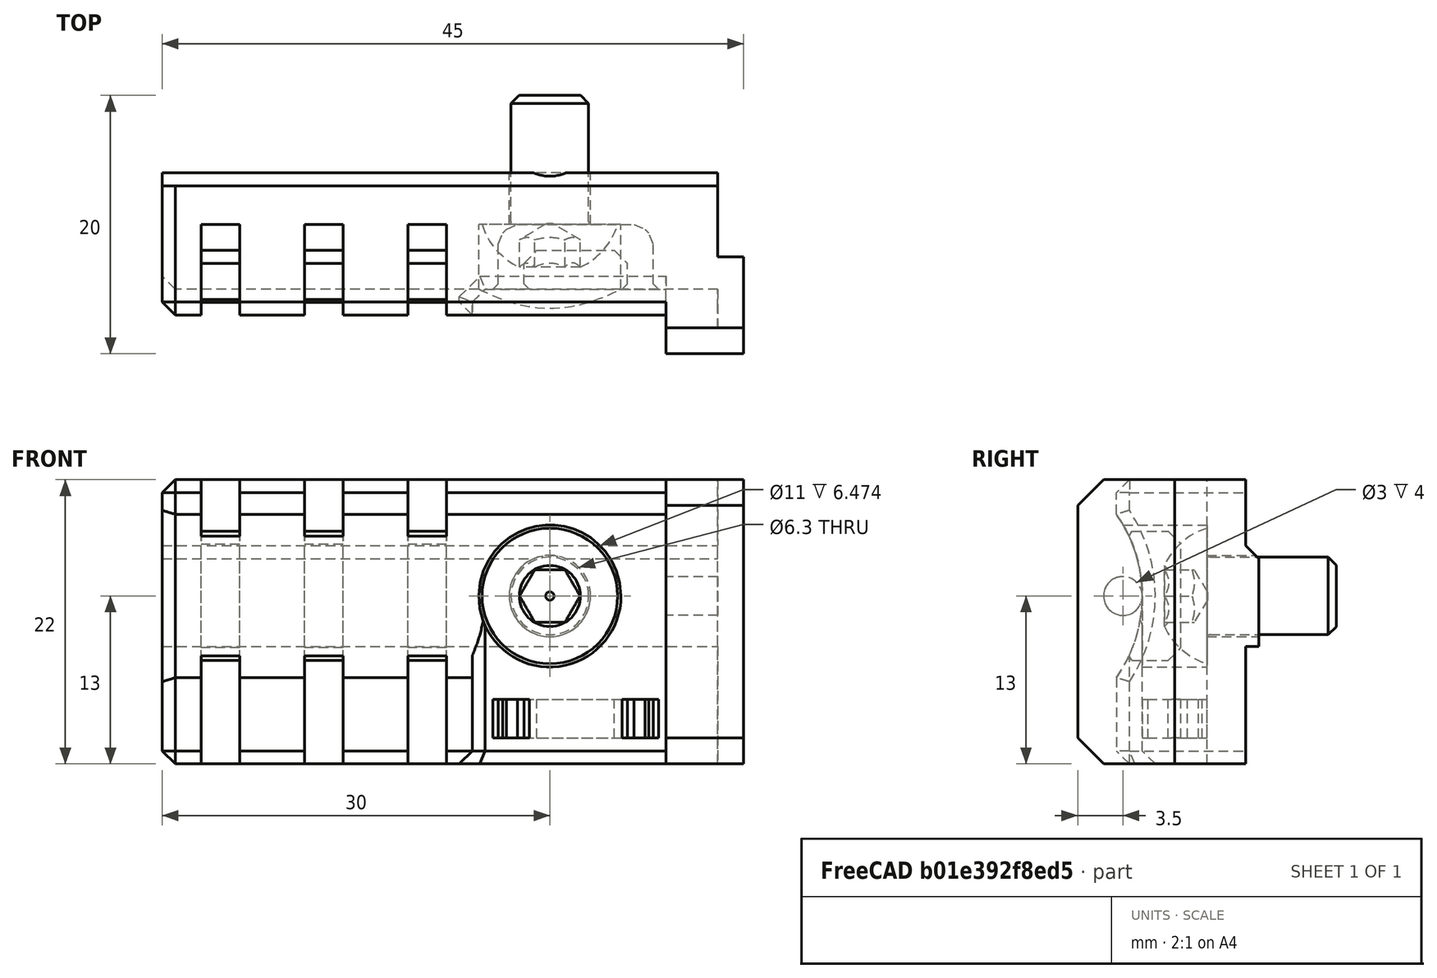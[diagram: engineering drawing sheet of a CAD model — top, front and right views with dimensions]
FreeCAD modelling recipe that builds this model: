
FCSTD DOCUMENT  (FreeCAD 0.19R24291 (Git))
Label: extruder-cable-end-assembly
License: Other
LicenseURL: GPL3
objects: Part::FeaturePython×1, Part::Feature×1, PartDesign::CoordinateSystem×1, App::Part×1
note: 3 computed .brp shape members not serialized (recipe doc carries the construction recipe); baked Part::Feature solids carry a one-line shape summary decoded from their .brp

FEATURE [Part::FeaturePython] Screw1384  label="M6x10-Screw"  # Fasteners workbench fastener (typed FeaturePython)
  Placement = pos=(-15,7,13) rot=(1,0,0;1.5708rad)
  diameter = 4
  invert = true
  length = 0
  lengthCustom = 10
  matchOuter = true
  offset = 0
  thread = false
  type = 39
FEATURE [Part::Feature] Chamfer009001004001001  label="extruder-cable-end-mounter"
  shape: bbox 45 x 14 x 22 mm, 100 faces (baked)
FEATURE [PartDesign::CoordinateSystem] LCS_extruder_cable_mounter  label="LCS_extruder-cable-mounter"
  AttacherType = Attacher::AttachEngine3D
FEATURE [App::Part] Part198  label="extruder-cable-mounter"
  Group = -> [Screw1384,Chamfer009001004001001,LCS_extruder_cable_mounter]
  Origin = -> Origin207
